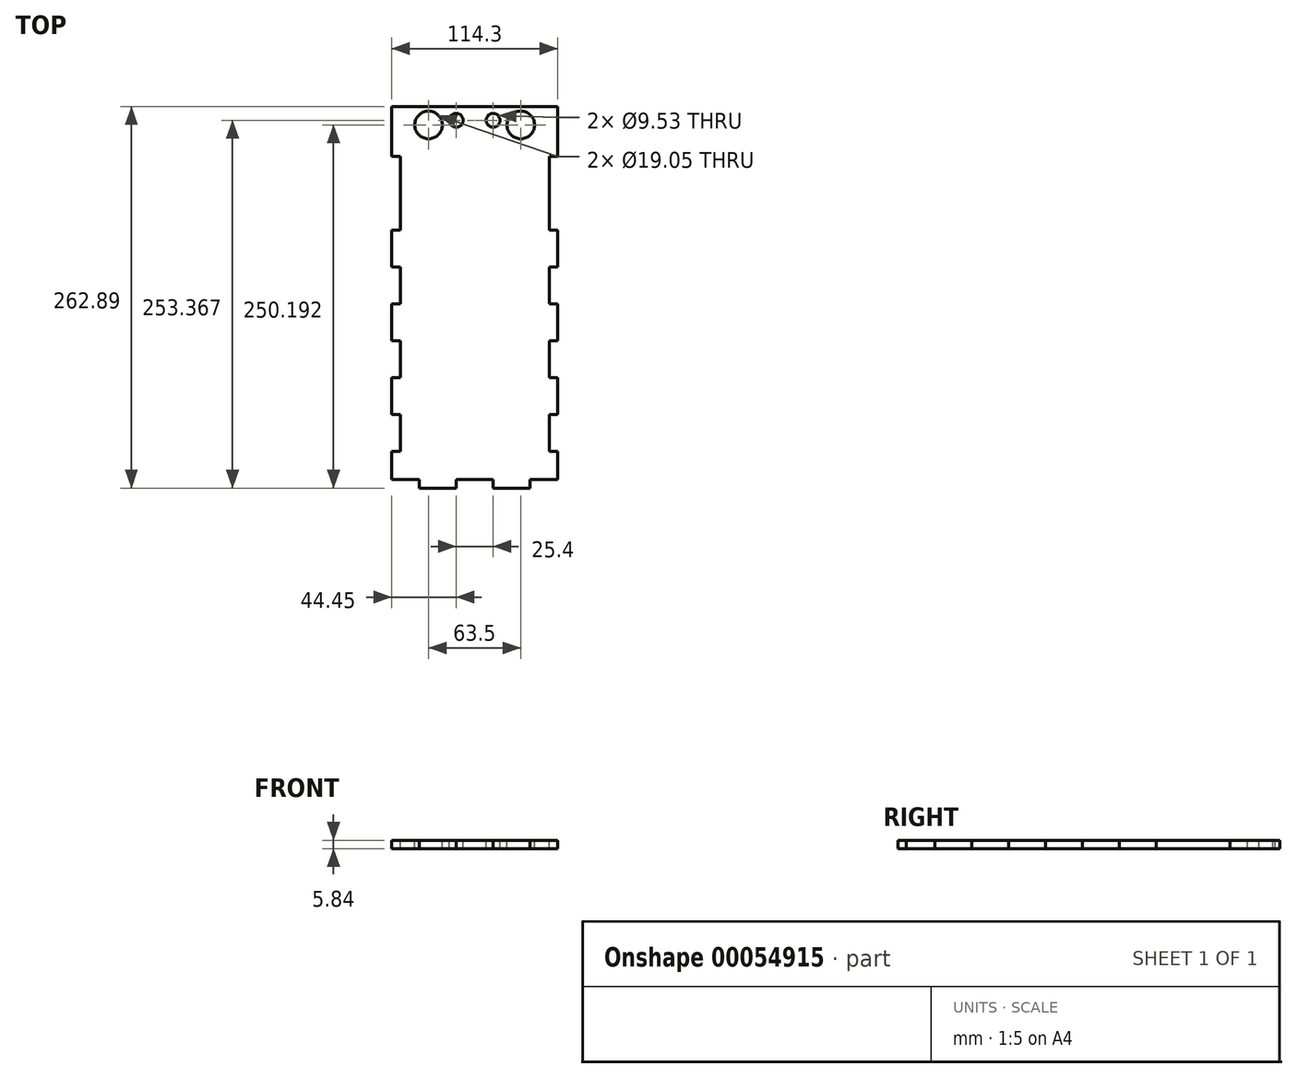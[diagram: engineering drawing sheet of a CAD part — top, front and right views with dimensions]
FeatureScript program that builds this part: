
annotation { "Feature Type Name" : "Feature", "Feature Type Description" : "" }
export const myFeature = defineFeature(function(context is Context, id is Id, definition is map)
    precondition{}
    {
        {
            var Q0;
            Q0=qCreatedBy(makeId("Top.planeOp"),FACE);
            var sketch = newSketch(context, id + "F0", { "sketchPlane" : qUnion([Q0])});
            skLineSegment(sketch, "E0.bottom", {"start": v(-78.46, -118.93) * mm, "end": v(35.84, -118.93) * mm});
            skLineSegment(sketch, "E0.top", {"start": v(-78.46, 143.96) * mm, "end": v(35.84, 143.96) * mm});
            skLineSegment(sketch, "E0.left", {"start": v(-78.46, -118.93) * mm, "end": v(-78.46, 143.96) * mm});
            skLineSegment(sketch, "E0.right", {"start": v(35.84, -118.93) * mm, "end": v(35.84, 143.96) * mm});
            skSolve(sketch);
        }
        {
            var Q0;
            Q0=makeQuery(id+"F0.imprint","IMPRINT",FACE,{"disambiguationData":[TD([[makeQuery(id+"F0.imprint","IMPRINT",EDGE,{"derivedFrom":sQuery(id+"F0.wireOp",EDGE,"E0.bottom")}),1.0]])]});
            extrude(context, id + "F1", {"entities" : qUnion([Q0]), "oppositeDirection" : true, "depth" : 5.84 * mm});
        }
        {
            var Q0;
            Q0=makeQuery(id+"F1.opExtrude","CAP_FACE",FACE,{"disambiguationData":[OSD([sQuery(id+"F0.wireOp",EDGE,"E0.bottom"),sQuery(id+"F0.wireOp",EDGE,"E0.top"),sQuery(id+"F0.wireOp",EDGE,"E0.left"),sQuery(id+"F0.wireOp",EDGE,"E0.right")])],"isStart":true});
            var sketch = newSketch(context, id + "F2", { "sketchPlane" : qUnion([Q0])});
            skLineSegment(sketch, "E1.bottom", {"start": v(-59.4, -118.93) * mm, "end": v(-34, -118.93) * mm});
            skLineSegment(sketch, "E1.top", {"start": v(-59.4, -113.09) * mm, "end": v(-34, -113.09) * mm});
            skLineSegment(sketch, "E1.left", {"start": v(-59.4, -118.93) * mm, "end": v(-59.4, -113.09) * mm});
            skLineSegment(sketch, "E1.right", {"start": v(-34, -118.93) * mm, "end": v(-34, -113.09) * mm});
            skLineSegment(sketch, "E2.bottom", {"start": v(16.8, -118.93) * mm, "end": v(-8.6, -118.93) * mm});
            skLineSegment(sketch, "E2.top", {"start": v(16.8, -113.09) * mm, "end": v(-8.6, -113.09) * mm});
            skLineSegment(sketch, "E2.left", {"start": v(16.8, -118.93) * mm, "end": v(16.8, -113.09) * mm});
            skLineSegment(sketch, "E2.right", {"start": v(-8.6, -118.93) * mm, "end": v(-8.6, -113.09) * mm});
            skLineSegment(sketch, "E3", {"start": v(-59.4, -113.09) * mm, "end": v(-78.46, -113.09) * mm});
            skLineSegment(sketch, "E4", {"start": v(-34, -113.09) * mm, "end": v(-8.6, -113.09) * mm});
            skLineSegment(sketch, "E5", {"start": v(16.8, -113.09) * mm, "end": v(35.84, -113.09) * mm});
            skLineSegment(sketch, "E6.bottom", {"start": v(-78.46, -93.53) * mm, "end": v(-72.62, -93.53) * mm});
            skLineSegment(sketch, "E6.top", {"start": v(-78.46, -68.13) * mm, "end": v(-72.62, -68.13) * mm});
            skLineSegment(sketch, "E6.left", {"start": v(-78.46, -93.53) * mm, "end": v(-78.46, -68.13) * mm});
            skLineSegment(sketch, "E6.right", {"start": v(-72.62, -93.53) * mm, "end": v(-72.62, -68.13) * mm});
            skLineSegment(sketch, "E7.bottom", {"start": v(-78.46, -42.73) * mm, "end": v(-72.62, -42.73) * mm});
            skLineSegment(sketch, "E7.top", {"start": v(-78.46, -17.33) * mm, "end": v(-72.62, -17.33) * mm});
            skLineSegment(sketch, "E7.left", {"start": v(-78.46, -42.73) * mm, "end": v(-78.46, -17.33) * mm});
            skLineSegment(sketch, "E7.right", {"start": v(-72.62, -42.73) * mm, "end": v(-72.62, -17.33) * mm});
            skLineSegment(sketch, "E8.bottom", {"start": v(-78.46, 8.07) * mm, "end": v(-72.62, 8.07) * mm});
            skLineSegment(sketch, "E8.top", {"start": v(-78.46, 33.47) * mm, "end": v(-72.62, 33.47) * mm});
            skLineSegment(sketch, "E8.left", {"start": v(-78.46, 8.07) * mm, "end": v(-78.46, 33.47) * mm});
            skLineSegment(sketch, "E8.right", {"start": v(-72.62, 8.07) * mm, "end": v(-72.62, 33.47) * mm});
            skLineSegment(sketch, "E9.bottom", {"start": v(35.84, -93.53) * mm, "end": v(30, -93.53) * mm});
            skLineSegment(sketch, "E9.top", {"start": v(35.84, -68.13) * mm, "end": v(30, -68.13) * mm});
            skLineSegment(sketch, "E9.left", {"start": v(35.84, -93.53) * mm, "end": v(35.84, -68.13) * mm});
            skLineSegment(sketch, "E9.right", {"start": v(30, -93.53) * mm, "end": v(30, -68.13) * mm});
            skLineSegment(sketch, "E10.bottom", {"start": v(35.84, -42.73) * mm, "end": v(30, -42.73) * mm});
            skLineSegment(sketch, "E10.top", {"start": v(35.84, -17.33) * mm, "end": v(30, -17.33) * mm});
            skLineSegment(sketch, "E10.left", {"start": v(35.84, -42.73) * mm, "end": v(35.84, -17.33) * mm});
            skLineSegment(sketch, "E10.right", {"start": v(30, -42.73) * mm, "end": v(30, -17.33) * mm});
            skLineSegment(sketch, "E11.bottom", {"start": v(35.84, 8.07) * mm, "end": v(30, 8.07) * mm});
            skLineSegment(sketch, "E11.top", {"start": v(35.84, 33.47) * mm, "end": v(30, 33.47) * mm});
            skLineSegment(sketch, "E11.left", {"start": v(35.84, 8.07) * mm, "end": v(35.84, 33.47) * mm});
            skLineSegment(sketch, "E11.right", {"start": v(30, 8.07) * mm, "end": v(30, 33.47) * mm});
            skLineSegment(sketch, "E12", {"start": v(-72.62, 33.47) * mm, "end": v(-72.62, 143.96) * mm});
            skLineSegment(sketch, "E13", {"start": v(30, 33.47) * mm, "end": v(30, 143.96) * mm});
            skLineSegment(sketch, "E14", {"start": v(30, 143.96) * mm, "end": v(-72.62, 143.96) * mm});
            skLineSegment(sketch, "E15.bottom", {"start": v(-72.62, 58.87) * mm, "end": v(-78.46, 58.87) * mm});
            skLineSegment(sketch, "E15.top", {"start": v(-72.62, 84.27) * mm, "end": v(-78.46, 84.27) * mm});
            skLineSegment(sketch, "E15.left", {"start": v(-72.62, 58.87) * mm, "end": v(-72.62, 84.27) * mm});
            skLineSegment(sketch, "E15.right", {"start": v(-78.46, 58.87) * mm, "end": v(-78.46, 84.27) * mm});
            skLineSegment(sketch, "E16.bottom", {"start": v(35.84, 58.87) * mm, "end": v(30, 58.87) * mm});
            skLineSegment(sketch, "E16.top", {"start": v(35.84, 84.27) * mm, "end": v(30, 84.27) * mm});
            skLineSegment(sketch, "E16.left", {"start": v(35.84, 58.87) * mm, "end": v(35.84, 84.27) * mm});
            skLineSegment(sketch, "E16.right", {"start": v(30, 58.87) * mm, "end": v(30, 84.27) * mm});
            skLineSegment(sketch, "E17.bottom", {"start": v(-72.62, 109.67) * mm, "end": v(-78.46, 109.67) * mm});
            skLineSegment(sketch, "E17.top", {"start": v(-72.62, 135.07) * mm, "end": v(-78.46, 135.07) * mm});
            skLineSegment(sketch, "E17.left", {"start": v(-72.62, 109.67) * mm, "end": v(-72.62, 135.07) * mm});
            skLineSegment(sketch, "E17.right", {"start": v(-78.46, 109.67) * mm, "end": v(-78.46, 135.07) * mm});
            skLineSegment(sketch, "E18.bottom", {"start": v(30, 135.07) * mm, "end": v(35.84, 135.07) * mm});
            skLineSegment(sketch, "E18.top", {"start": v(30, 109.67) * mm, "end": v(35.84, 109.67) * mm});
            skLineSegment(sketch, "E18.left", {"start": v(30, 135.07) * mm, "end": v(30, 109.67) * mm});
            skLineSegment(sketch, "E18.right", {"start": v(35.84, 135.07) * mm, "end": v(35.84, 109.67) * mm});
            skSolve(sketch);
        }
        {
            var Q0;
            {var subQ0=sQuery(id+"F2.wireOp",EDGE,"E1.right");Q0=makeQuery(id+"F2.imprint","IMPRINT",FACE,{"disambiguationData":[TD([[makeQuery(id+"F2.imprint","IMPRINT",EDGE,{"derivedFrom":subQ0}),-1.0]])]});}
            var Q1;
            {var subQ0=sQuery(id+"F2.wireOp",EDGE,"E1.left");Q1=makeQuery(id+"F2.imprint","IMPRINT",FACE,{"disambiguationData":[TD([[makeQuery(id+"F2.imprint","IMPRINT",EDGE,{"derivedFrom":subQ0}),1.0]])]});}
            var Q2;
            {var subQ0=sQuery(id+"F2.wireOp",EDGE,"E2.left");Q2=makeQuery(id+"F2.imprint","IMPRINT",FACE,{"disambiguationData":[TD([[makeQuery(id+"F2.imprint","IMPRINT",EDGE,{"derivedFrom":subQ0}),-1.0]])]});}
            var Q3;
            Q3=makeQuery(id+"F2.imprint","IMPRINT",FACE,{"disambiguationData":[TD([[makeQuery(id+"F2.imprint","IMPRINT",EDGE,{"derivedFrom":sQuery(id+"F2.wireOp",EDGE,"E6.bottom")}),1.0]])]});
            var Q4;
            Q4=makeQuery(id+"F2.imprint","IMPRINT",FACE,{"disambiguationData":[TD([[makeQuery(id+"F2.imprint","IMPRINT",EDGE,{"derivedFrom":sQuery(id+"F2.wireOp",EDGE,"E9.bottom")}),-1.0]])]});
            var Q5;
            Q5=makeQuery(id+"F2.imprint","IMPRINT",FACE,{"disambiguationData":[TD([[makeQuery(id+"F2.imprint","IMPRINT",EDGE,{"derivedFrom":sQuery(id+"F2.wireOp",EDGE,"E10.bottom")}),-1.0]])]});
            var Q6;
            Q6=makeQuery(id+"F2.imprint","IMPRINT",FACE,{"disambiguationData":[TD([[makeQuery(id+"F2.imprint","IMPRINT",EDGE,{"derivedFrom":sQuery(id+"F2.wireOp",EDGE,"E7.bottom")}),1.0]])]});
            var Q7;
            Q7=makeQuery(id+"F2.imprint","IMPRINT",FACE,{"disambiguationData":[TD([[makeQuery(id+"F2.imprint","IMPRINT",EDGE,{"derivedFrom":sQuery(id+"F2.wireOp",EDGE,"E8.bottom")}),1.0]])]});
            var Q8;
            Q8=makeQuery(id+"F2.imprint","IMPRINT",FACE,{"disambiguationData":[TD([[makeQuery(id+"F2.imprint","IMPRINT",EDGE,{"derivedFrom":sQuery(id+"F2.wireOp",EDGE,"E11.bottom")}),-1.0]])]});
            var Q9;
            Q9=makeQuery(id+"F2.imprint","IMPRINT",FACE,{"disambiguationData":[TD([[makeQuery(id+"F2.imprint","IMPRINT",EDGE,{"derivedFrom":sQuery(id+"F2.wireOp",EDGE,"5ee332e6-36f6-4adf-a736-26aea6b07d2d.bottom")}),1.0]])]});
            var Q10;
            Q10=makeQuery(id+"F2.imprint","IMPRINT",FACE,{"disambiguationData":[TD([[makeQuery(id+"F2.imprint","IMPRINT",EDGE,{"derivedFrom":sQuery(id+"F2.wireOp",EDGE,"6ff9eec2-7fa8-49e7-8809-b80a6dbca018.bottom")}),-1.0]])]});
            var Q11;
            Q11=makeQuery(id+"F2.imprint","IMPRINT",FACE,{"disambiguationData":[TD([[makeQuery(id+"F2.imprint","IMPRINT",EDGE,{"derivedFrom":sQuery(id+"F2.wireOp",EDGE,"E15.bottom")}),-1.0]])]});
            var Q12;
            Q12=makeQuery(id+"F2.imprint","IMPRINT",FACE,{"disambiguationData":[TD([[makeQuery(id+"F2.imprint","IMPRINT",EDGE,{"derivedFrom":sQuery(id+"F2.wireOp",EDGE,"E16.bottom")}),-1.0]])]});
            var Q13;
            {var subQ0=sQuery(id+"F2.wireOp",EDGE,"E15.top");Q13=makeQuery(id+"F2.imprint","IMPRINT",FACE,{"disambiguationData":[TD([[makeQuery(id+"F2.imprint","IMPRINT",EDGE,{"derivedFrom":subQ0}),-1.0]])]});}
            var Q14;
            {var subQ0=sQuery(id+"F2.wireOp",EDGE,"E16.top");Q14=makeQuery(id+"F2.imprint","IMPRINT",FACE,{"disambiguationData":[TD([[makeQuery(id+"F2.imprint","IMPRINT",EDGE,{"derivedFrom":subQ0}),-1.0]])]});}
            var Q15;
            Q15=makeQuery(id+"F1.opExtrude","CAP_FACE",FACE,{"disambiguationData":[OSD([sQuery(id+"F0.wireOp",EDGE,"E0.bottom"),sQuery(id+"F0.wireOp",EDGE,"E0.top"),sQuery(id+"F0.wireOp",EDGE,"E0.left"),sQuery(id+"F0.wireOp",EDGE,"E0.right")])],"isStart":false});
            extrude(context, id + "F3", {"entities" : qUnion([Q0, Q1, Q2, Q3, Q4, Q5, Q6, Q7, Q8, Q9, Q10, Q11, Q12, Q13, Q14]), "operationType" : NewBodyOperationType.REMOVE, "endBound" : BoundingType.UP_TO_SURFACE, "oppositeDirection" : true, "endBoundEntityFace" : qUnion([Q15]), "depth" : 25.4 * mm});
        }
        {
            var Q0;
            Q0=makeQuery(id+"F1.opExtrude","CAP_FACE",FACE,{"disambiguationData":[OSD([sQuery(id+"F0.wireOp",EDGE,"E0.bottom"),sQuery(id+"F0.wireOp",EDGE,"E0.top"),sQuery(id+"F0.wireOp",EDGE,"E0.left"),sQuery(id+"F0.wireOp",EDGE,"E0.right")])],"isStart":true});
            var sketch = newSketch(context, id + "F4", { "sketchPlane" : qUnion([Q0])});
            skCircle(sketch, "E19", {"center": v(-34, 134.44) * mm, "radius": 4.76 * mm});
            skCircle(sketch, "E20", {"center": v(-8.6, 134.44) * mm, "radius": 4.76 * mm});
            skLineSegment(sketch, "E21", {"start": v(-34, 134.44) * mm, "end": v(-8.6, 134.44) * mm, "construction": true});
            skPoint(sketch, "E22", {"position": v(-21.3, 134.44) * mm});
            skPoint(sketch, "E23", {"position": v(-21.3, 143.96) * mm});
            skCircle(sketch, "E24", {"center": v(-53.06, 131.26) * mm, "radius": 9.53 * mm});
            skCircle(sketch, "E25", {"center": v(10.44, 131.26) * mm, "radius": 9.53 * mm});
            skLineSegment(sketch, "E26", {"start": v(-53.06, 131.26) * mm, "end": v(10.44, 131.26) * mm, "construction": true});
            skPoint(sketch, "E27", {"position": v(-21.3, 131.26) * mm});
            skSolve(sketch);
        }
        {
            var Q0;
            Q0=makeQuery(id+"F4.imprint","IMPRINT",FACE,{"disambiguationData":[TD([[makeQuery(id+"F4.imprint","IMPRINT",EDGE,{"derivedFrom":sQuery(id+"F4.wireOp",EDGE,"E19")}),1.0]])]});
            var Q1;
            Q1=makeQuery(id+"F4.imprint","IMPRINT",FACE,{"disambiguationData":[TD([[makeQuery(id+"F4.imprint","IMPRINT",EDGE,{"derivedFrom":sQuery(id+"F4.wireOp",EDGE,"E20")}),1.0]])]});
            var Q2;
            Q2=makeQuery(id+"F4.imprint","IMPRINT",FACE,{"disambiguationData":[TD([[makeQuery(id+"F4.imprint","IMPRINT",EDGE,{"derivedFrom":sQuery(id+"F4.wireOp",EDGE,"E24")}),1.0]])]});
            var Q3;
            Q3=makeQuery(id+"F4.imprint","IMPRINT",FACE,{"disambiguationData":[TD([[makeQuery(id+"F4.imprint","IMPRINT",EDGE,{"derivedFrom":sQuery(id+"F4.wireOp",EDGE,"E25")}),1.0]])]});
            var Q4;
            Q4=makeQuery(id+"F1.opExtrude","CAP_FACE",FACE,{"disambiguationData":[OSD([sQuery(id+"F0.wireOp",EDGE,"E0.bottom"),sQuery(id+"F0.wireOp",EDGE,"E0.top"),sQuery(id+"F0.wireOp",EDGE,"E0.left"),sQuery(id+"F0.wireOp",EDGE,"E0.right")])],"isStart":false});
            extrude(context, id + "F5", {"entities" : qUnion([Q0, Q1, Q2, Q3]), "operationType" : NewBodyOperationType.REMOVE, "endBound" : BoundingType.UP_TO_SURFACE, "oppositeDirection" : true, "endBoundEntityFace" : qUnion([Q4]), "depth" : 25.4 * mm});
        }
    });
